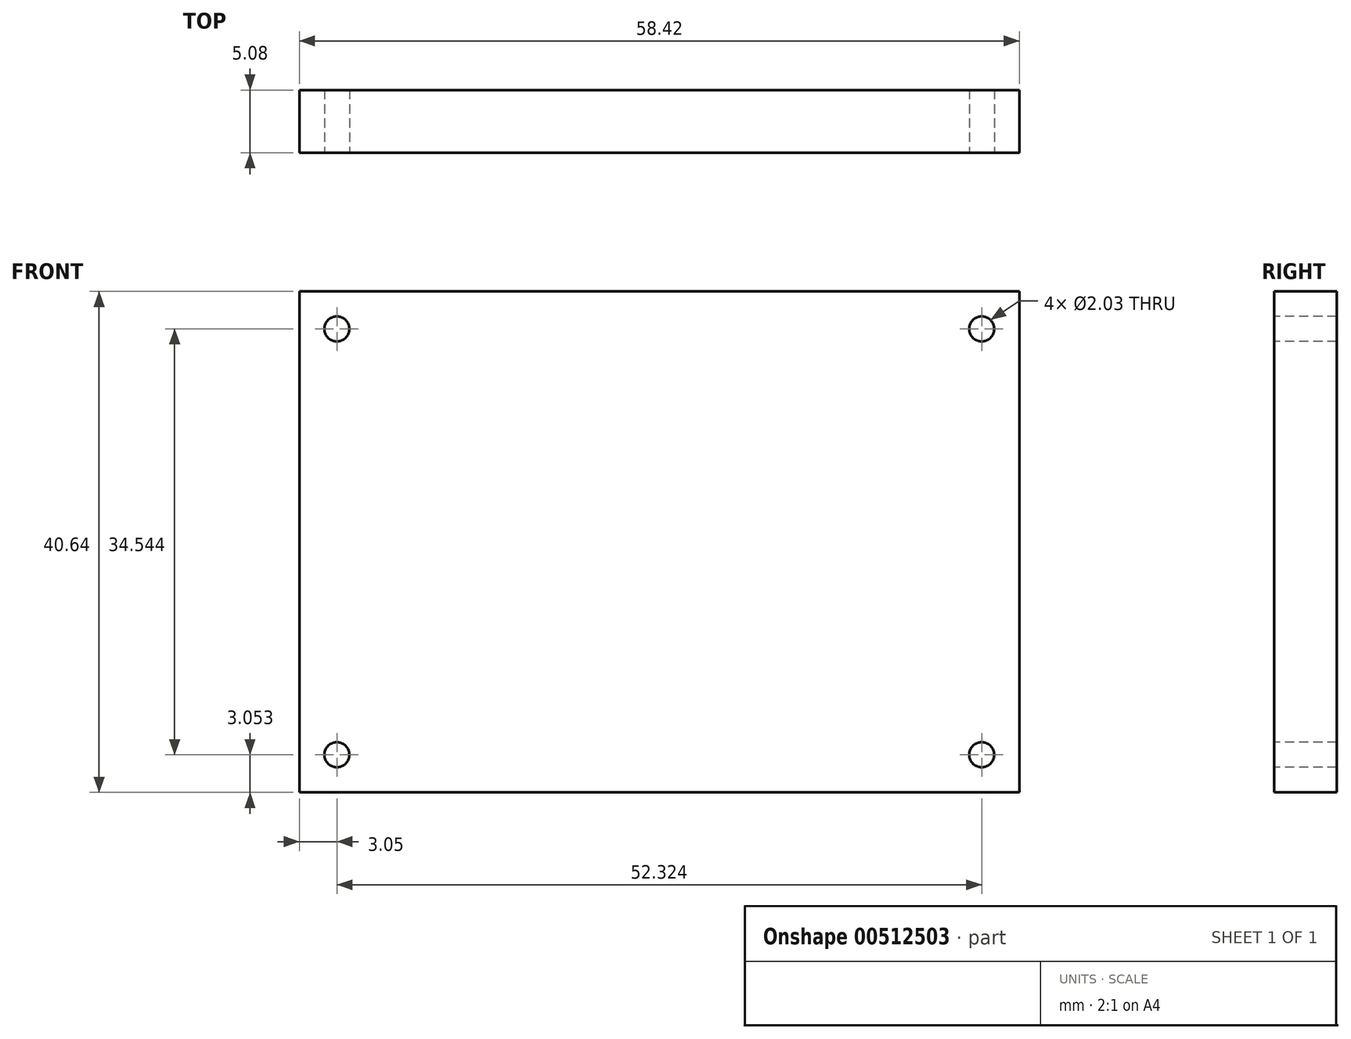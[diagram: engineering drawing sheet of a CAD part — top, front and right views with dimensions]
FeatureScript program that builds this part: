
annotation { "Feature Type Name" : "Feature", "Feature Type Description" : "" }
export const myFeature = defineFeature(function(context is Context, id is Id, definition is map)
    precondition{}
    {
        {
            var Q0;
            Q0=qCreatedBy(makeId("Front.planeOp"),FACE);
            var sketch = newSketch(context, id + "F0", { "sketchPlane" : qUnion([Q0])});
            skLineSegment(sketch, "E0.bottom", {"start": v(-42.37, 40.37) * mm, "end": v(16.05, 40.37) * mm});
            skLineSegment(sketch, "E0.top", {"start": v(-42.37, -0.27) * mm, "end": v(16.05, -0.27) * mm});
            skLineSegment(sketch, "E0.left", {"start": v(-42.37, 40.37) * mm, "end": v(-42.37, -0.27) * mm});
            skLineSegment(sketch, "E0.right", {"start": v(16.05, 40.37) * mm, "end": v(16.05, -0.27) * mm});
            skSolve(sketch);
        }
        {
            var Q0;
            Q0=makeQuery(id+"F0.imprint","IMPRINT",FACE,{"disambiguationData":[TD([[makeQuery(id+"F0.imprint","IMPRINT",EDGE,{"derivedFrom":sQuery(id+"F0.wireOp",EDGE,"E0.bottom")}),-1.0]])]});
            extrude(context, id + "F1", {"entities" : qUnion([Q0]), "depth" : 5.08 * mm, "offsetDistance" : 25.4 * mm});
        }
        {
            var Q0;
            Q0=makeQuery(id+"F1.opExtrude","CAP_FACE",FACE,{"disambiguationData":[OSD([sQuery(id+"F0.wireOp",EDGE,"E0.bottom"),sQuery(id+"F0.wireOp",EDGE,"E0.top"),sQuery(id+"F0.wireOp",EDGE,"E0.left"),sQuery(id+"F0.wireOp",EDGE,"E0.right")])],"isStart":false});
            var sketch = newSketch(context, id + "F2", { "sketchPlane" : qUnion([Q0])});
            skCircle(sketch, "E1", {"center": v(-39.32, 37.33) * mm, "radius": 1.02 * mm});
            skCircle(sketch, "E2.MirrorC", {"center": v(-39.32, 2.78) * mm, "radius": 1.02 * mm});
            skCircle(sketch, "E3.MirrorC", {"center": v(13, 37.33) * mm, "radius": 1.02 * mm});
            skCircle(sketch, "E4.MirrorC", {"center": v(13, 2.78) * mm, "radius": 1.02 * mm});
            skSolve(sketch);
        }
        {
            var Q0;
            Q0 = qSketchRegion(id + "F2", true);
            extrude(context, id + "F3", {"entities" : qUnion([Q0]), "operationType" : NewBodyOperationType.REMOVE, "oppositeDirection" : true, "depth" : 25.4 * mm, "offsetDistance" : 25.4 * mm});
        }
    });
